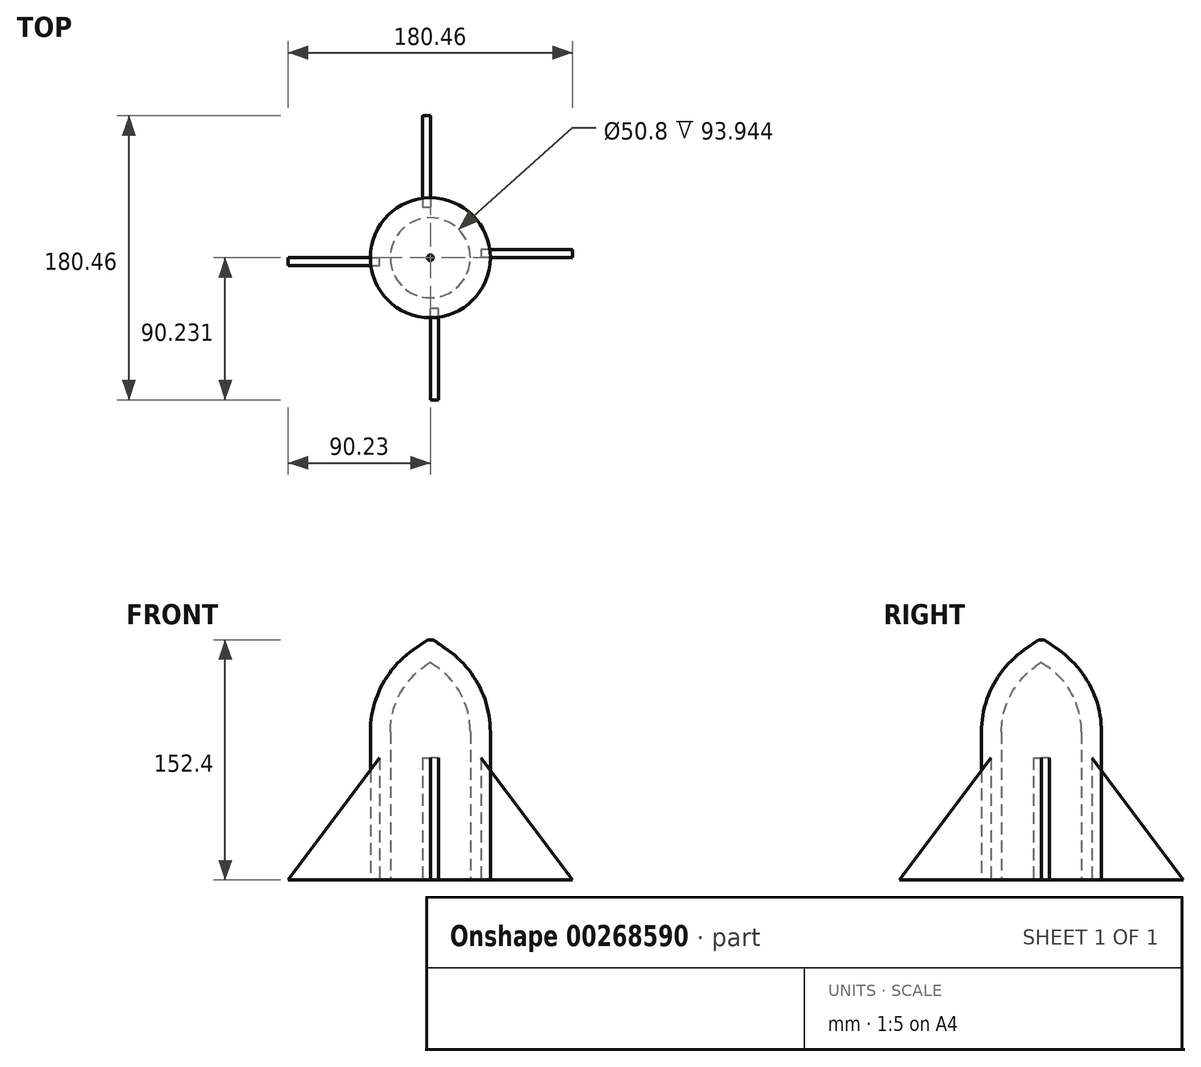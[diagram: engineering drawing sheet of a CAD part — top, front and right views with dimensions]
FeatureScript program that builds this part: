
annotation { "Feature Type Name" : "Feature", "Feature Type Description" : "" }
export const myFeature = defineFeature(function(context is Context, id is Id, definition is map)
    precondition{}
    {
        {
            var Q0;
            Q0=qCreatedBy(makeId("Top.planeOp"),FACE);
            var sketch = newSketch(context, id + "F0", { "sketchPlane" : qUnion([Q0])});
            skCircle(sketch, "E0", {"center": v(0, -2.44) * mm, "radius": 38.1 * mm});
            skSolve(sketch);
        }
        {
            var Q0;
            Q0 = qSketchRegion(id + "F0", true);
            extrude(context, id + "F1", {"entities" : qUnion([Q0]), "depth" : 127 * mm});
        }
        {
            var Q0;
            Q0=makeQuery(id+"F1.opExtrude","CAP_FACE",FACE,{"disambiguationData":[OSD([sQuery(id+"F0.wireOp",EDGE,"E0")])],"isStart":false});
            var sketch = newSketch(context, id + "F2", { "sketchPlane" : qUnion([Q0])});
            skSolve(sketch);
        }
        {
            var Q0;
            Q0=makeQuery(id+"F2.imprint","IMPRINT",FACE,{"disambiguationData":[TD([[makeQuery(id+"F2.imprint","IMPRINT",EDGE,{"derivedFrom":makeQuery(id+"F1.opExtrude","CAP_EDGE",EDGE,{"disambiguationData":[OSD([sQuery(id+"F0.wireOp",EDGE,"E0")])],"isStart":false})}),1.0]])]});
            extrude(context, id + "F3", {"entities" : qUnion([Q0]), "operationType" : NewBodyOperationType.ADD, "depth" : 25.4 * mm, "hasDraft" : true, "draftAngle" : 55 * degree, "draftPullDirection" : true});
        }
        {
            var Q0;
            {var subQ0=sQuery(id+"F0.wireOp",EDGE,"E0");Q0=makeQuery(id+"F3.boolean.opBoolean","MERGE",EDGE,{"derivedFrom":[makeQuery(id+"F1.opExtrude","CAP_EDGE",EDGE,{"disambiguationData":[OSD([subQ0])],"isStart":false}),makeQuery(id+"F3.opExtrude","CAP_EDGE",EDGE,{"disambiguationData":[OSD([subQ0])],"isStart":true})]});}
            fillet(context, id + "F4", {"entities" : qUnion([Q0]), "radius" : 63.5 * mm, "tangentPropagation" : true, "allowEdgeOverflow" : false});
        }
        {
            var Q0;
            Q0=makeQuery(id+"F1.opExtrude","CAP_FACE",FACE,{"disambiguationData":[OSD([sQuery(id+"F0.wireOp",EDGE,"E0")])],"isStart":true});
            shell(context, id + "F5", {"entities" : qUnion([Q0]), "thickness" : 12.7 * mm});
        }
        {
            var Q0;
            Q0=qCreatedBy(makeId("Right.planeOp"),FACE);
            var sketch = newSketch(context, id + "F6", { "sketchPlane" : qUnion([Q0])});
            skLineSegment(sketch, "E1", {"start": v(-34.55, 77.42) * mm, "end": v(-34.55, 0) * mm});
            skLineSegment(sketch, "E2", {"start": v(-92.67, 0) * mm, "end": v(-34.55, 77.42) * mm});
            skLineSegment(sketch, "E3", {"start": v(-92.67, 0) * mm, "end": v(-34.55, 0) * mm});
            skSolve(sketch);
        }
        {
            var Q0;
            Q0 = qSketchRegion(id + "F6", true);
            extrude(context, id + "F7", {"entities" : qUnion([Q0]), "depth" : 5.08 * mm});
        }
        {
            var Q0;
            Q0=makeQuery(id+"F7.opExtrude","SWEPT_BODY",BODY,{"disambiguationData":[OSD([sQuery(id+"F6.wireOp",EDGE,"E1"),sQuery(id+"F6.wireOp",EDGE,"E2"),sQuery(id+"F6.wireOp",EDGE,"E3")])]});
            var Q1;
            Q1=makeQuery(id+"F1.opExtrude","CAP_EDGE",EDGE,{"disambiguationData":[OSD([sQuery(id+"F0.wireOp",EDGE,"E0")])],"isStart":true});
            circularPattern(context, id + "F8", {"entities" : qUnion([Q0]), "axis" : qUnion([Q1]), "angle" : 360 * degree, "instanceCount" : 4, "equalSpace" : true});
        }
    });
